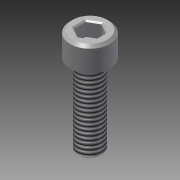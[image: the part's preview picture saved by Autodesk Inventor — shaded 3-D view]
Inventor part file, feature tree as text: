
AUTODESK INVENTOR PART (.ipt)
format: ipt  version: 2014 SP1 (Build 180222100, 222)  size: 92,672 bytes
history: native  units: in
note: dims shown in document units (in); Inventor stores cm internally (conversion verified against a paired STEP export)
features: other x2, thread x1, imported_body x1
ambient origin geometry x8: Origin, YZ Plane, XZ Plane, XY Plane, X Axis, Y Axis, Z Axis, Center Point
bodies: Body1 (feature_tree)
feature tree (4):
  other  "10-32x0625_shcs"
  other  "10-32x0625_shcs1"
  thread  "Thread1"  [1 undecoded]
  imported_body  "Base1"
note: 1 required parameter value undecoded (feature->parameter linkage not recoverable at this tier; creation-order binding heuristic only, values carry confidence <= 0.55)
